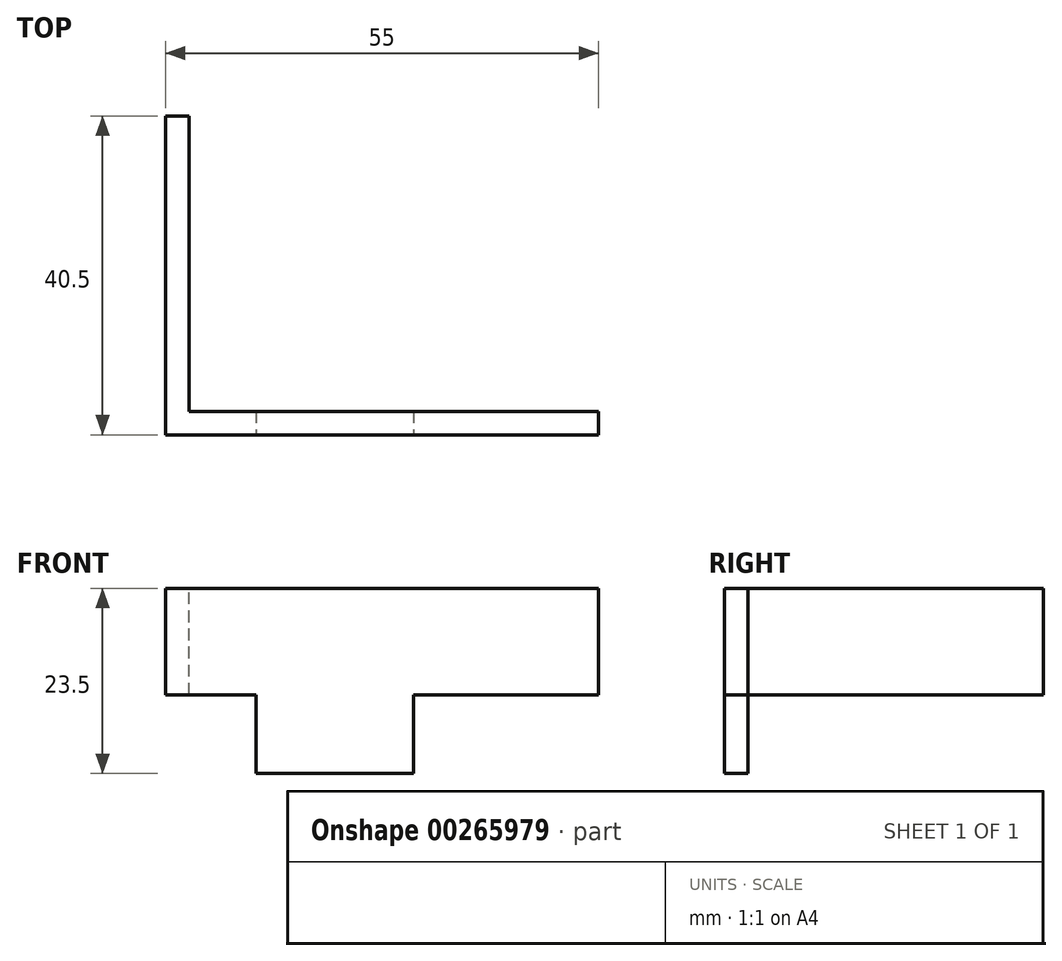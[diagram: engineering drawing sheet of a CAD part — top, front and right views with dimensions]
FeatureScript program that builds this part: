
annotation { "Feature Type Name" : "Feature", "Feature Type Description" : "" }
export const myFeature = defineFeature(function(context is Context, id is Id, definition is map)
    precondition{}
    {
        {
            var Q0;
            Q0=qCreatedBy(makeId("Front.planeOp"),FACE);
            var sketch = newSketch(context, id + "F0", { "sketchPlane" : qUnion([Q0])});
            skLineSegment(sketch, "E0.bottom", {"start": v(0, 0) * mm, "end": v(52, 0) * mm});
            skLineSegment(sketch, "E0.top", {"start": v(0, 13.5) * mm, "end": v(52, 13.5) * mm});
            skLineSegment(sketch, "E0.left", {"start": v(0, 0) * mm, "end": v(0, 13.5) * mm});
            skLineSegment(sketch, "E0.right", {"start": v(52, 0) * mm, "end": v(52, 13.5) * mm});
            skSolve(sketch);
        }
        {
            var Q0;
            Q0=makeQuery(id+"F0.imprint","IMPRINT",FACE,{"disambiguationData":[TD([[makeQuery(id+"F0.imprint","IMPRINT",EDGE,{"derivedFrom":sQuery(id+"F0.wireOp",EDGE,"E0.bottom")}),1.0]])]});
            extrude(context, id + "F1", {"entities" : qUnion([Q0]), "depth" : 3 * mm, "offsetDistance" : 25 * mm});
        }
        {
            var Q0;
            Q0=makeQuery(id+"F1.opExtrude","SWEPT_FACE",FACE,{"disambiguationData":[OSD([sQuery(id+"F0.wireOp",EDGE,"E0.left")])]});
            var sketch = newSketch(context, id + "F2", { "sketchPlane" : qUnion([Q0])});
            skPoint(sketch, "E1.oppositeSnap0", {"position": v(1.5, 13.5) * mm});
            skLineSegment(sketch, "E1.bottom", {"start": v(3, 0) * mm, "end": v(-37.5, 0) * mm});
            skLineSegment(sketch, "E1.top", {"start": v(3, 13.5) * mm, "end": v(-37.5, 13.5) * mm});
            skLineSegment(sketch, "E1.left", {"start": v(3, 0) * mm, "end": v(3, 13.5) * mm});
            skLineSegment(sketch, "E1.right", {"start": v(-37.5, 0) * mm, "end": v(-37.5, 13.5) * mm});
            skSolve(sketch);
        }
        {
            var Q0;
            {var subQ2=sQuery(id+"F2.wireOp",EDGE,"E1.right");Q0=makeQuery(id+"F2.imprint","IMPRINT",FACE,{"disambiguationData":[TD([[makeQuery(id+"F2.imprint","IMPRINT",EDGE,{"derivedFrom":subQ2}),-1.0]])]});}
            var Q1;
            {var subQ2=sQuery(id+"F2.wireOp",EDGE,"E1.left");Q1=makeQuery(id+"F2.imprint","IMPRINT",FACE,{"disambiguationData":[TD([[makeQuery(id+"F2.imprint","IMPRINT",EDGE,{"derivedFrom":subQ2}),1.0]])]});}
            extrude(context, id + "F3", {"entities" : qUnion([Q0, Q1]), "operationType" : NewBodyOperationType.ADD, "depth" : 3 * mm, "offsetDistance" : 25 * mm});
        }
        {
            var Q0;
            Q0=makeQuery(id+"F3.boolean.opBoolean","MERGE",FACE,{"derivedFrom":[makeQuery(id+"F1.opExtrude","CAP_FACE",FACE,{"disambiguationData":[OSD([sQuery(id+"F0.wireOp",EDGE,"E0.bottom"),sQuery(id+"F0.wireOp",EDGE,"E0.top"),sQuery(id+"F0.wireOp",EDGE,"E0.left"),sQuery(id+"F0.wireOp",EDGE,"E0.right")])],"isStart":false}),makeQuery(id+"F3.opExtrude","SWEPT_FACE",FACE,{"disambiguationData":[OSD([sQuery(id+"F2.wireOp",EDGE,"E1.left")])]})]});
            var sketch = newSketch(context, id + "F4", { "sketchPlane" : qUnion([Q0])});
            skLineSegment(sketch, "E2.bottom", {"start": v(8.5, 0) * mm, "end": v(28.5, 0) * mm});
            skLineSegment(sketch, "E2.top", {"start": v(8.5, -10) * mm, "end": v(28.5, -10) * mm});
            skLineSegment(sketch, "E2.left", {"start": v(8.5, 0) * mm, "end": v(8.5, -10) * mm});
            skLineSegment(sketch, "E2.right", {"start": v(28.5, 0) * mm, "end": v(28.5, -10) * mm});
            skSolve(sketch);
        }
        {
            var Q0;
            Q0=makeQuery(id+"F4.imprint","IMPRINT",FACE,{"disambiguationData":[TD([[makeQuery(id+"F4.imprint","IMPRINT",EDGE,{"derivedFrom":sQuery(id+"F4.wireOp",EDGE,"E2.bottom")}),-1.0]])]});
            extrude(context, id + "F5", {"entities" : qUnion([Q0]), "operationType" : NewBodyOperationType.ADD, "oppositeDirection" : true, "depth" : 3 * mm, "offsetDistance" : 25 * mm});
        }
    });
